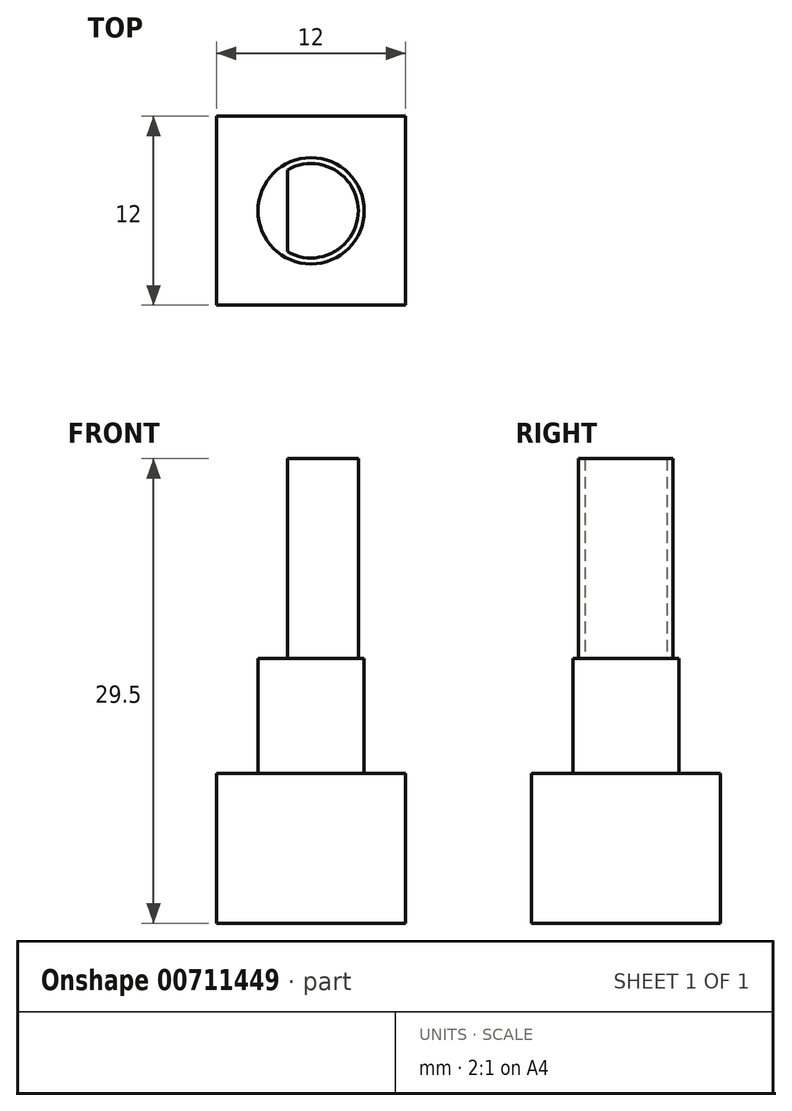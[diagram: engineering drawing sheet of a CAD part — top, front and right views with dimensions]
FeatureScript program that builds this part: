
annotation { "Feature Type Name" : "Feature", "Feature Type Description" : "" }
export const myFeature = defineFeature(function(context is Context, id is Id, definition is map)
    precondition{}
    {
        {
            var Q0;
            Q0=qCreatedBy(makeId("Top.planeOp"),FACE);
            var sketch = newSketch(context, id + "F0", { "sketchPlane" : qUnion([Q0])});
            skLineSegment(sketch, "E0.bottom", {"start": v(6, -6) * mm, "end": v(-6, -6) * mm});
            skLineSegment(sketch, "E0.top", {"start": v(6, 6) * mm, "end": v(-6, 6) * mm});
            skLineSegment(sketch, "E0.left", {"start": v(6, -6) * mm, "end": v(6, 6) * mm});
            skLineSegment(sketch, "E0.right", {"start": v(-6, -6) * mm, "end": v(-6, 6) * mm});
            skPoint(sketch, "E0.middle", {"position": v(0, 0) * mm});
            skCircle(sketch, "E1", {"center": v(0, 0) * mm, "radius": 3.38 * mm});
            skCircle(sketch, "E2", {"center": v(0, 0) * mm, "radius": 3 * mm});
            skLineSegment(sketch, "E3", {"start": v(-1.5, 2.6) * mm, "end": v(-1.5, -2.6) * mm});
            skSolve(sketch);
        }
        {
            var Q0;
            Q0=makeQuery(id+"F0.imprint","IMPRINT",FACE,{"disambiguationData":[TD([[makeQuery(id+"F0.imprint","IMPRINT",EDGE,{"derivedFrom":sQuery(id+"F0.wireOp",EDGE,"E0.bottom")}),-1.0]])]});
            var Q1;
            {var subQ0=sQuery(id+"F0.wireOp",EDGE,"E3");Q1=makeQuery(id+"F0.imprint","IMPRINT",FACE,{"disambiguationData":[TD([[makeQuery(id+"F0.imprint","IMPRINT",EDGE,{"derivedFrom":subQ0}),1.0]])]});}
            var Q2;
            {var subQ0=sQuery(id+"F0.wireOp",EDGE,"E3");Q2=makeQuery(id+"F0.imprint","IMPRINT",FACE,{"disambiguationData":[TD([[makeQuery(id+"F0.imprint","IMPRINT",EDGE,{"derivedFrom":subQ0}),-1.0]])]});}
            var Q3;
            Q3=makeQuery(id+"F0.imprint","IMPRINT",FACE,{"disambiguationData":[TD([[makeQuery(id+"F0.imprint","IMPRINT",EDGE,{"derivedFrom":sQuery(id+"F0.wireOp",EDGE,"E1")}),1.0]])]});
            extrude(context, id + "F1", {"entities" : qUnion([Q0, Q1, Q2, Q3]), "oppositeDirection" : true, "depth" : 9.5 * mm, "offsetDistance" : 25 * mm});
        }
        {
            var Q0;
            Q0=makeQuery(id+"F0.imprint","IMPRINT",FACE,{"disambiguationData":[TD([[makeQuery(id+"F0.imprint","IMPRINT",EDGE,{"derivedFrom":sQuery(id+"F0.wireOp",EDGE,"E1")}),1.0]])]});
            var Q1;
            {var subQ0=sQuery(id+"F0.wireOp",EDGE,"E3");Q1=makeQuery(id+"F0.imprint","IMPRINT",FACE,{"disambiguationData":[TD([[makeQuery(id+"F0.imprint","IMPRINT",EDGE,{"derivedFrom":subQ0}),1.0]])]});}
            var Q2;
            {var subQ0=sQuery(id+"F0.wireOp",EDGE,"E3");Q2=makeQuery(id+"F0.imprint","IMPRINT",FACE,{"disambiguationData":[TD([[makeQuery(id+"F0.imprint","IMPRINT",EDGE,{"derivedFrom":subQ0}),-1.0]])]});}
            extrude(context, id + "F2", {"entities" : qUnion([Q0, Q1, Q2]), "operationType" : NewBodyOperationType.ADD, "depth" : 7.3 * mm, "offsetDistance" : 25 * mm});
        }
        {
            var Q0;
            {var subQ0=sQuery(id+"F0.wireOp",EDGE,"E3");Q0=makeQuery(id+"F0.imprint","IMPRINT",FACE,{"disambiguationData":[TD([[makeQuery(id+"F0.imprint","IMPRINT",EDGE,{"derivedFrom":subQ0}),1.0]])]});}
            extrude(context, id + "F3", {"entities" : qUnion([Q0]), "operationType" : NewBodyOperationType.ADD, "depth" : 20 * mm, "offsetDistance" : 25 * mm});
        }
    });
